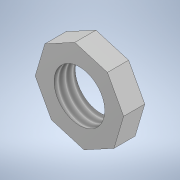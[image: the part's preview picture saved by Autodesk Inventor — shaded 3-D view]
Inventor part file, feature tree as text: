
AUTODESK INVENTOR PART (.ipt)
format: ipt  version: 2021 (Build 250183000, 183)  size: 112,128 bytes
history: native  units: in
note: dims shown in document units (in); Inventor stores cm internally (conversion verified against a paired STEP export)
features: other x2, thread x1
ambient origin geometry x8: Origin, YZ Plane, XZ Plane, XY Plane, X Axis, Y Axis, Z Axis, Center Point
bodies: Body1 (feature_tree)
feature tree (3):
  other  "Sólido2"
  thread  "Rosca1"  [1 undecoded]
  other  "Sólido1"
note: 1 required parameter value undecoded (feature->parameter linkage not recoverable at this tier; creation-order binding heuristic only, values carry confidence <= 0.55)
